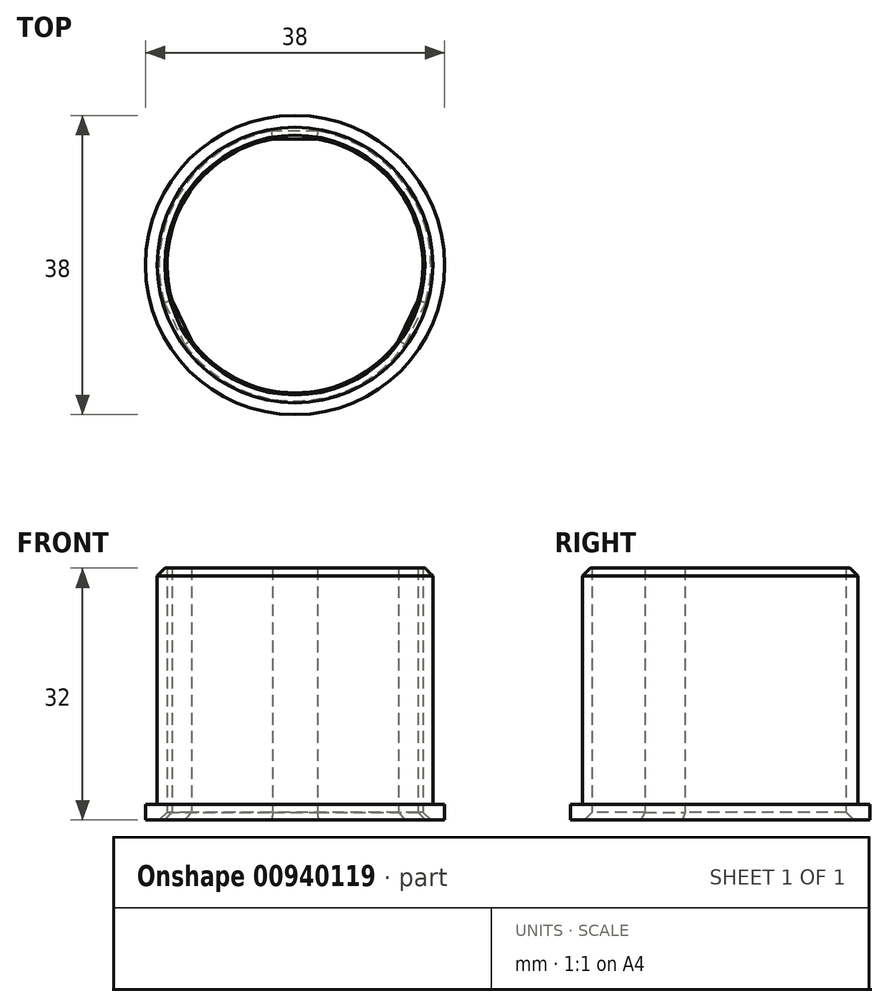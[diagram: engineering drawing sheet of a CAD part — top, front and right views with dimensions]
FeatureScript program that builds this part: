
annotation { "Feature Type Name" : "Feature", "Feature Type Description" : "" }
export const myFeature = defineFeature(function(context is Context, id is Id, definition is map)
    precondition{}
    {
        {
            var Q0;
            Q0=qCreatedBy(makeId("Top.planeOp"),FACE);
            var sketch = newSketch(context, id + "F0", { "sketchPlane" : qUnion([Q0])});
            skCircle(sketch, "E0", {"center": v(0, 0) * mm, "radius": 17.5 * mm});
            skArc(sketch, "E1", {"start": v(-2.84, 16) * mm, "mid": v(-13.78, 8.61) * mm, "end": v(-15.63, -4.45) * mm});
            skLineSegment(sketch, "E2", {"start": v(-2.84, 16) * mm, "end": v(2.84, 16) * mm});
            skLineSegment(sketch, "E3", {"start": v(0, 0) * mm, "end": v(-20.51, -11.84) * mm, "construction": true});
            skLineSegment(sketch, "E4", {"start": v(-15.63, -4.45) * mm, "end": v(-13.14, -9.56) * mm});
            skArc(sketch, "E5.trimOffspring", {"start": v(-13.14, -9.56) * mm, "mid": v(0, -16.25) * mm, "end": v(13.14, -9.56) * mm});
            skPoint(sketch, "E6.MirrorCS.end.orphan", {"position": v(13.14, -9.56) * mm});
            skPoint(sketch, "E6.MirrorCS.start.orphan", {"position": v(15.63, -4.45) * mm});
            skLineSegment(sketch, "E7", {"start": v(13.14, -9.56) * mm, "end": v(15.63, -4.45) * mm});
            skArc(sketch, "E8.trimOffspring", {"start": v(15.63, -4.45) * mm, "mid": v(13.78, 8.61) * mm, "end": v(2.84, 16) * mm});
            skSolve(sketch);
        }
        {
            var Q0;
            Q0 = qSketchRegion(id + "F0", true);
            extrude(context, id + "F1", {"entities" : qUnion([Q0]), "depth" : 30 * mm, "offsetDistance" : 25 * mm});
        }
        {
            var Q0;
            Q0=makeQuery(id+"F1.opExtrude","CAP_FACE",FACE,{"disambiguationData":[OSD([sQuery(id+"F0.wireOp",EDGE,"E0"),sQuery(id+"F0.wireOp",EDGE,"E1"),sQuery(id+"F0.wireOp",EDGE,"E2"),sQuery(id+"F0.wireOp",EDGE,"E4"),sQuery(id+"F0.wireOp",EDGE,"E5.trimOffspring"),sQuery(id+"F0.wireOp",EDGE,"E7"),sQuery(id+"F0.wireOp",EDGE,"E8.trimOffspring")])],"isStart":true});
            var sketch = newSketch(context, id + "F2", { "sketchPlane" : qUnion([Q0])});
            skCircle(sketch, "E9", {"center": v(0, 0) * mm, "radius": 19 * mm});
            skArc(sketch, "E10.0", {"start": v(-13.14, 9.56) * mm, "mid": v(0, 16.25) * mm, "end": v(13.14, 9.56) * mm});
            skLineSegment(sketch, "E11.0", {"start": v(-15.63, 4.45) * mm, "end": v(-13.14, 9.56) * mm});
            skArc(sketch, "E12.0", {"start": v(-2.84, -16) * mm, "mid": v(-13.78, -8.61) * mm, "end": v(-15.63, 4.45) * mm});
            skLineSegment(sketch, "E13.0", {"start": v(-2.84, -16) * mm, "end": v(2.84, -16) * mm});
            skArc(sketch, "E14.0", {"start": v(15.63, 4.45) * mm, "mid": v(13.78, -8.61) * mm, "end": v(2.84, -16) * mm});
            skPoint(sketch, "E15.0", {"position": v(14.38, 7) * mm});
            skLineSegment(sketch, "E16.0", {"start": v(13.14, 9.56) * mm, "end": v(15.63, 4.45) * mm});
            skSolve(sketch);
        }
        {
            var Q0;
            Q0 = qSketchRegion(id + "F2", true);
            extrude(context, id + "F3", {"entities" : qUnion([Q0]), "operationType" : NewBodyOperationType.ADD, "depth" : 2 * mm, "offsetDistance" : 25 * mm});
        }
        {
            var Q0;
            Q0=makeQuery(id+"F1.opExtrude","CAP_EDGE",EDGE,{"disambiguationData":[OSD([sQuery(id+"F0.wireOp",EDGE,"E0")])],"isStart":false});
            chamfer(context, id + "F4", {"entities" : qUnion([Q0]), "width" : 1 * mm, "tangentPropagation" : true});
        }
        {
            var Q0;
            Q0=makeQuery(id+"F3.opExtrude","CAP_EDGE",EDGE,{"disambiguationData":[OSD([sQuery(id+"F2.wireOp",EDGE,"E10.0")])],"isStart":false});
            var Q1;
            Q1=makeQuery(id+"F3.opExtrude","CAP_EDGE",EDGE,{"disambiguationData":[OSD([sQuery(id+"F2.wireOp",EDGE,"E16.0")])],"isStart":false});
            var Q2;
            Q2=makeQuery(id+"F3.opExtrude","CAP_EDGE",EDGE,{"disambiguationData":[OSD([sQuery(id+"F2.wireOp",EDGE,"E14.0")])],"isStart":false});
            var Q3;
            Q3=makeQuery(id+"F3.opExtrude","CAP_EDGE",EDGE,{"disambiguationData":[OSD([sQuery(id+"F2.wireOp",EDGE,"E13.0")])],"isStart":false});
            var Q4;
            Q4=makeQuery(id+"F3.opExtrude","CAP_EDGE",EDGE,{"disambiguationData":[OSD([sQuery(id+"F2.wireOp",EDGE,"E12.0")])],"isStart":false});
            var Q5;
            Q5=makeQuery(id+"F3.opExtrude","CAP_EDGE",EDGE,{"disambiguationData":[OSD([sQuery(id+"F2.wireOp",EDGE,"E11.0")])],"isStart":false});
            chamfer(context, id + "F5", {"entities" : qUnion([Q0, Q1, Q2, Q3, Q4, Q5]), "width" : 1 * mm, "tangentPropagation" : true});
        }
    });
